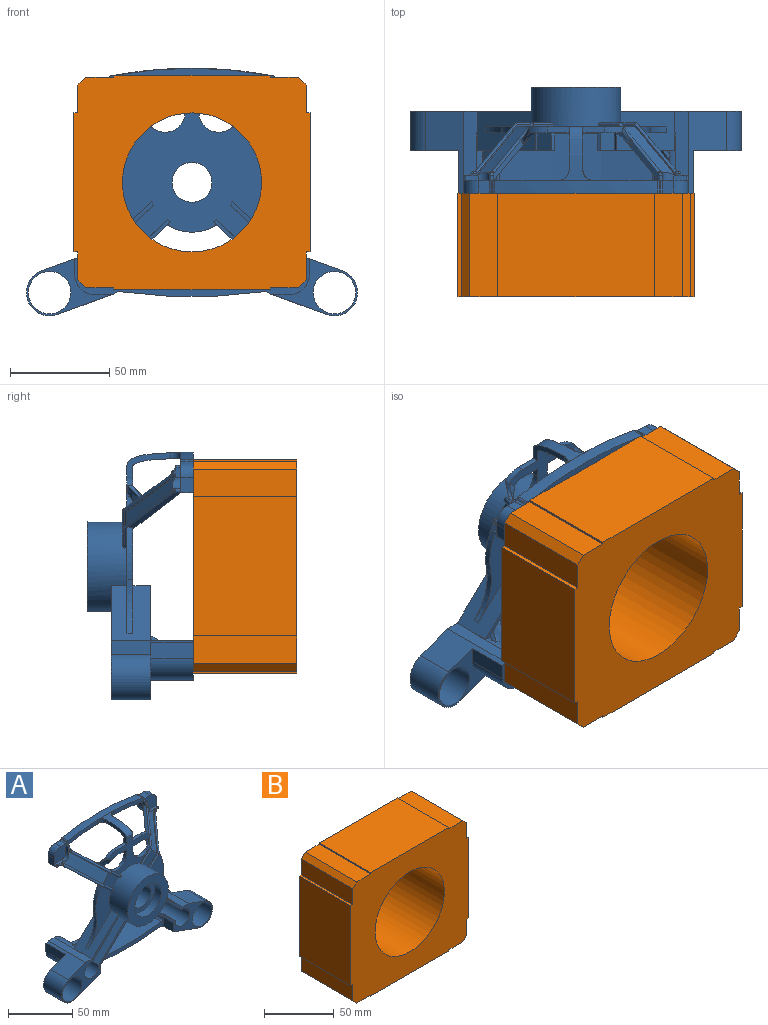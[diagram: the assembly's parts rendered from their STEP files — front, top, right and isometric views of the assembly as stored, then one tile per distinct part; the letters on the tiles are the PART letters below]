
ASSEMBLY  parts=2 mates=1
PART A: 213 faces, bbox 167x53.9x125 mm
  f0: plane 29.84x28.32mm, normal (-0.69,0,-0.73), area 460.5mm2, adj f3,f12,f15,f169,f198,f201,f211
  f1: plane 24.48x23.23mm, normal (0.69,0,0.73), area 266.4mm2, adj f92,f164,f202,f212
  f2: plane 29.8x28.28mm, normal (0.69,0,0.73), area 459.4mm2, adj f12,f15,f169,f198,f201,f202,f211
  f3: plane 30.33x28.26mm, normal (0,1,0), area 78.6mm2, adj f0,f162,f163,f169,f195,f209
  f4: bspline ~14.26x14.19mm, area 140.4mm2, adj f6,f8,f161,f205,f206,f208
  f5: bspline ~14.26x14.22mm, area 139.4mm2, adj f6,f161,f183,f205,f206,f208
  f6: plane 29.84x28.32mm, normal (0.69,0,-0.73), area 739.5mm2, adj f4,f5,f8,f12,f14,f92,f159,f183
  f7: plane 29.59x28.88mm, normal (0,1,0), area 78.6mm2, adj f68,f160,f161,f171,f183,f205
  f8: cylinder r=7.75mm len=33mm, axis (0,1,0), area 1335.2mm2, adj f4,f6,f161,f192,f204
  f9: plane 41.51x6.78mm, normal (0,0,1), area 271.3mm2, adj f11,f169,f195,f199,f201
  f10: plane 41.51x6.78mm, normal (0,0,1), area 271.3mm2, adj f11,f183,f188,f189,f192
  f11: plane 118x20mm, normal (0,1,0), area 921.6mm2, adj f9,f10,f166,f167,f168,f169,f170,f171
  f12: cylinder r=22.5mm len=45mm, axis (0,1,0), area 2748.5mm2, adj f0,f2,f6,f13,f14,f15,f16,f30
  f13: plane 53.41x25.44mm, normal (0,-1,0), area 518.2mm2, adj f12,f90,f91,f117,f135,f136,f188
  f14: plane 25.41x24.79mm, normal (0,-1,0), area 265.4mm2, adj f6,f12,f161,f207
  f15: plane 25.41x24.79mm, normal (0,-1,0), area 265.3mm2, adj f0,f2,f12,f211
  f16: plane 25.18x5.2mm, normal (0,-1,0), area 60.8mm2, adj f12,f68,f69,f70
  f17: bspline ~29.85x28.26mm, area 350.7mm2, adj f18,f19,f31,f65,f66,f149,f151,f154
  f18: plane 2x0.59mm, normal (0,-1,0), area 0.4mm2, adj f17,f65,f141
  f19: plane 2x0.59mm, normal (0,-1,0), area 0.4mm2, adj f17,f66,f140
  f20: plane 2x0.59mm, normal (0,-1,0), area 0.4mm2, adj f25,f61,f121
  f21: bspline ~29.85x28.16mm, area 455.1mm2, adj f44,f45,f46,f92,f97,f98,f102
  f22: bspline ~29.85x28.26mm, area 457.5mm2, adj f50,f51,f52,f92,f99,f100,f110
  f23: plane 2.67x2mm, normal (0,-1,0), area 2.7mm2, adj f50,f66,f67,f147
  f24: plane 3.69x2mm, normal (0,-1,0), area 4.7mm2, adj f52,f64,f65,f146
  f25: bspline ~28.25x26.47mm, area 380.2mm2, adj f20,f28,f33,f61,f62,f130,f132,f153
  f26: plane 3.69x2mm, normal (0,-1,0), area 4.7mm2, adj f44,f62,f63,f129
  f27: plane 2.67x2mm, normal (0,-1,0), area 2.7mm2, adj f46,f60,f61,f128
  f28: plane 2x0.59mm, normal (0,-1,0), area 0.4mm2, adj f25,f29,f62
  f29: cylinder r=2mm len=1.41mm, axis (0,1,0), area 1.6mm2, adj f28,f62,f124,f132,f137
  f30: plane 46.67x31.07mm, normal (0,-1,0), area 530.7mm2, adj f12,f74,f75,f76,f77,f78,f79,f80
  f31: plane 16.76x16.52mm, normal (0,-1,0), area 131.9mm2, adj f12,f17,f118,f120
  f32: plane 53.41x25.45mm, normal (0,-1,0), area 518.2mm2, adj f12,f71,f72,f73,f119,f148,f150,f195
  f33: plane 16.76x16.52mm, normal (0,-1,0), area 131.9mm2, adj f12,f25,f115,f116
  f34: plane 113x19.44mm, normal (0,-1,0), area 550.8mm2, adj f37,f38,f39,f40,f41,f42,f43,f46
  f35: plane 1x1mm, normal (0,-1,0), area 0.2mm2, adj f52,f53,f64
  f36: plane 1x1mm, normal (0,-1,0), area 0.2mm2, adj f43,f44,f63
  f37: cylinder r=216.01mm len=81.79mm, axis (0,1,0), area 534.9mm2, adj f34,f38,f58,f59
  f38: cylinder r=2mm len=6.5mm, axis (0,1,0), area 7.7mm2, adj f34,f37,f39,f59
  f39: plane 6.5x0.4mm, normal (-0.71,0,0.71), area 3.6mm2, adj f34,f38,f40,f59
  f40: cylinder r=2mm len=6.5mm, axis (0,1,0), area 10.2mm2, adj f34,f39,f41,f59
  f41: plane 6.5x5.26mm, normal (0,0,1), area 34.2mm2, adj f34,f40,f42,f59
  f42: cylinder r=7.5mm len=7.5mm, axis (0,1,0), area 76.6mm2, adj f34,f41,f43,f59
  f43: plane 7.5x6.5mm, normal (-1,0,0), area 48.7mm2, adj f34,f36,f42,f44,f59
  f44: plane 10x7.5mm, normal (0,0,-1), area 61.7mm2, adj f21,f26,f36,f43,f45,f59,f63,f97
  f45: cylinder r=7.5mm len=8.02mm, axis (0,1,0), area 94.3mm2, adj f21,f44,f46,f59
  f46: plane 10x5.49mm, normal (1,0,0), area 34.5mm2, adj f21,f27,f34,f45,f47,f59,f60,f98
  f47: cylinder r=2mm len=6.5mm, axis (0,1,0), area 18mm2, adj f34,f46,f48,f59
  f48: cylinder r=212.51mm len=79.75mm, axis (0,1,0), area 521.5mm2, adj f34,f47,f49,f59
  f49: cylinder r=2mm len=6.5mm, axis (0,1,0), area 18mm2, adj f34,f48,f50,f59
  f50: plane 10x5.49mm, normal (-1,0,0), area 34.5mm2, adj f22,f23,f34,f49,f51,f59,f67,f100
  f51: cylinder r=7.5mm len=8.02mm, axis (0,1,0), area 94.3mm2, adj f22,f50,f52,f59
  f52: plane 10x7.5mm, normal (0,0,-1), area 61.7mm2, adj f22,f24,f35,f51,f53,f59,f64,f99
  f53: plane 7.5x6.5mm, normal (1,0,0), area 48.7mm2, adj f34,f35,f52,f54,f59
  f54: cylinder r=7.5mm len=7.5mm, axis (0,1,0), area 76.6mm2, adj f34,f53,f55,f59
  f55: plane 6.5x5.26mm, normal (0,0,1), area 34.2mm2, adj f34,f54,f56,f59
  f56: cylinder r=2mm len=6.5mm, axis (0,1,0), area 10.2mm2, adj f34,f55,f57,f59
  f57: plane 6.5x0.4mm, normal (0.71,0,0.71), area 3.6mm2, adj f34,f56,f58,f59
  f58: cylinder r=2mm len=6.5mm, axis (0,1,0), area 7.7mm2, adj f34,f37,f57,f59
  f59: plane 113x20.44mm, normal (0,1,0), area 697.2mm2, adj f37,f38,f39,f40,f41,f42,f43,f44
  f60: cylinder r=1mm len=2.5mm, axis (0,1,0), area 7.9mm2, adj f27,f34,f46,f61
  f61: plane 5.48x3.5mm, normal (-1,0,0), area 14.7mm2, adj f20,f25,f27,f34,f60,f121,f126,f128
  f62: plane 6.5x3.5mm, normal (0,0,1), area 17.2mm2, adj f25,f26,f28,f29,f34,f63,f127,f129
  f63: cylinder r=1mm len=2.5mm, axis (0,1,0), area 7.9mm2, adj f26,f34,f36,f44,f62
  f64: cylinder r=1mm len=2.5mm, axis (0,1,0), area 7.9mm2, adj f24,f34,f35,f52,f65
  f65: plane 6.5x3.5mm, normal (0,0,1), area 17.2mm2, adj f17,f18,f24,f34,f64,f141,f144,f146
  f66: plane 5.48x3.5mm, normal (1,0,0), area 14.7mm2, adj f17,f19,f23,f34,f67,f140,f145,f147
  f67: cylinder r=1mm len=2.5mm, axis (0,1,0), area 7.9mm2, adj f23,f34,f50,f66
  f68: plane 29.31x27.81mm, normal (0.69,0,-0.73), area 800.2mm2, adj f7,f12,f16,f69,f92,f160,f171,f192
  f69: cylinder r=25mm len=25.18mm, axis (0,1,0), area 79.2mm2, adj f16,f68,f70,f92
  f70: plane 29.31x27.81mm, normal (-0.69,0,-0.73), area 800.2mm2, adj f12,f16,f69,f92,f164,f170,f201,f202
  f71: cylinder r=30mm len=27.1mm, axis (0,1,0), area 89.2mm2, adj f32,f72,f92,f195
  f72: cylinder r=37.5mm len=26.29mm, axis (0,1,0), area 82mm2, adj f32,f71,f73,f92,f99,f150
  f73: plane 0.07x0.06mm, normal (-0.67,0,0.74), area 0mm2, adj f32,f72,f150
  f74: plane 10.44x9.5mm, normal (-0.67,0,0.74), area 19.5mm2, adj f12,f30,f75,f92,f100,f138
  f75: cylinder r=10mm len=16.73mm, axis (0,1,0), area 69.3mm2, adj f30,f74,f76,f92
  f76: plane 4.74x3mm, normal (1,0,0), area 14.2mm2, adj f30,f75,f77,f92
  f77: plane 10.87x3mm, normal (0,0,-1), area 32.6mm2, adj f30,f76,f78,f92
  f78: cylinder r=7.5mm len=5.55mm, axis (0,1,0), area 18.7mm2, adj f30,f77,f92,f111,f114
  f79: cylinder r=12.5mm len=9.25mm, axis (0,1,0), area 31.2mm2, adj f30,f80,f92,f109,f114
  f80: plane 10.87x3mm, normal (0,0,1), area 32.6mm2, adj f30,f79,f81,f92
  f81: plane 22.18x12.25mm, normal (1,0,0), area 83.4mm2, adj f30,f80,f92,f155,f156,f157
  f82: plane 22.18x12.25mm, normal (-1,0,0), area 83.4mm2, adj f30,f83,f92,f155,f156,f158
  f83: plane 10.87x3mm, normal (0,0,1), area 32.6mm2, adj f30,f82,f84,f92
  f84: cylinder r=12.5mm len=9.25mm, axis (0,1,0), area 31.2mm2, adj f30,f83,f92,f103,f107
  f85: cylinder r=7.5mm len=5.55mm, axis (0,1,0), area 18.7mm2, adj f30,f86,f92,f101,f107
  f86: plane 10.87x3mm, normal (0,0,-1), area 32.6mm2, adj f30,f85,f87,f92
  f87: plane 4.74x3mm, normal (-1,0,0), area 14.2mm2, adj f30,f86,f88,f92
  f88: cylinder r=10mm len=16.73mm, axis (0,1,0), area 69.3mm2, adj f30,f87,f89,f92
  f89: plane 10.44x9.5mm, normal (0.67,0,0.74), area 19.5mm2, adj f12,f30,f88,f92,f98,f123
  f90: cylinder r=37.5mm len=26.39mm, axis (0,1,0), area 82.3mm2, adj f13,f91,f92,f97,f133,f134,f136
  f91: cylinder r=30mm len=27.1mm, axis (0,1,0), area 89.2mm2, adj f13,f90,f92,f188
  f92: plane 91.55x86.89mm, normal (0,1,0), area 3812.8mm2, adj f1,f6,f21,f22,f68,f69,f70,f71
  f93: cylinder r=14.5mm len=29mm, axis (0,1,0), area 637.7mm2, adj f94,f96
  f94: plane 45x45mm, normal (0,-1,0), area 929.9mm2, adj f12,f93
  f95: cylinder r=10mm len=20mm, axis (0,1,0), area 1005.3mm2, adj f92,f96
  f96: plane 29x29mm, normal (0,-1,0), area 346.4mm2, adj f93,f95
  f97: plane 25.78x20.52mm, normal (-0.66,0,-0.75), area 72.2mm2, adj f21,f44,f90,f92,f133
  f98: plane 28x19.95mm, normal (0.67,0,0.74), area 85.5mm2, adj f21,f46,f89,f104,f105,f106,f131
  f99: plane 26.81x20.43mm, normal (0.67,0,-0.74), area 98.4mm2, adj f22,f52,f72,f92,f150
  f100: plane 28x19.95mm, normal (-0.67,0,0.74), area 85.6mm2, adj f22,f50,f74,f108,f112,f113,f152
  f101: bspline ~6.29x5.94mm, area 15.6mm2, adj f85,f102,f104,f106,f107
  f102: bspline ~10.77x8.19mm, area 44mm2, adj f21,f92,f101,f103,f105,f106
  f103: bspline ~9.34x7.12mm, area 17.2mm2, adj f84,f102,f104,f105,f107
  f104: bspline ~9.52x9.23mm, area 44.3mm2, adj f98,f101,f103,f105,f106,f107
  f105: bspline ~3.15x2.78mm, area 2.4mm2, adj f98,f102,f103,f104
  f106: bspline ~3.26x2.86mm, area 4mm2, adj f98,f101,f102,f104
  f107: bspline ~5.9x5.51mm, area 3.4mm2, adj f30,f84,f85,f101,f103,f104
  f108: bspline ~10.31x8.72mm, area 43.2mm2, adj f100,f109,f111,f112,f113,f114
  f109: bspline ~8.62x7.66mm, area 16.9mm2, adj f79,f108,f110,f113,f114
  f110: bspline ~11.26x7.54mm, area 42.7mm2, adj f22,f92,f109,f111,f112,f113
  f111: bspline ~6.78x5.28mm, area 16.1mm2, adj f78,f108,f110,f112,f114
  f112: bspline ~3.12x2.62mm, area 3.7mm2, adj f100,f108,f110,f111
  f113: bspline ~3.17x2.74mm, area 2.8mm2, adj f100,f108,f109,f110
  f114: bspline ~5.51x5.14mm, area 3.1mm2, adj f30,f78,f79,f108,f109,f111
  f115: plane 10.03x9.13mm, normal (-0.67,0,-0.74), area 13.6mm2, adj f12,f33,f123,f130
  f116: plane 10.03x9.13mm, normal (0.67,0,0.74), area 13.6mm2, adj f12,f33,f122,f137
  f117: plane 10.44x9.5mm, normal (-0.67,0,-0.74), area 14.1mm2, adj f12,f13,f122,f135
  f118: plane 10.03x9.13mm, normal (-0.67,0,0.74), area 13.6mm2, adj f12,f31,f139,f149
  f119: plane 10.44x9.5mm, normal (0.67,0,-0.74), area 14.1mm2, adj f12,f32,f139,f148
  f120: plane 10.03x9.13mm, normal (0.67,0,-0.74), area 13.6mm2, adj f12,f31,f138,f151
  f121: cylinder r=2mm len=1.41mm, axis (0,1,0), area 1.6mm2, adj f20,f61,f125,f130
  f122: cylinder r=1mm len=11.79mm, axis (-0.74,0,0.67), area 43.4mm2, adj f12,f116,f117,f136
  f123: cylinder r=1mm len=11.79mm, axis (-0.74,0,0.67), area 43.4mm2, adj f12,f89,f115,f131
  f124: torus R=1mm, axis (0,-1,0), area 2.5mm2, adj f29,f127,f136
  f125: torus R=1mm, axis (0,1,0), area 2.5mm2, adj f121,f126,f131
  f126: torus R=1mm, axis (1,0,0), area 4mm2, adj f46,f61,f125,f128
  f127: torus R=1mm, axis (0,0,1), area 4mm2, adj f44,f62,f124,f129
  f128: cylinder r=1mm len=2.12mm, axis (0,-0.71,-0.71), area 5.1mm2, adj f27,f46,f61,f126
  f129: cylinder r=1mm len=2.12mm, axis (0.71,-0.71,0), area 5.1mm2, adj f26,f44,f62,f127
  f130: plane 25.5x20.02mm, normal (-0.67,0,-0.74), area 26.9mm2, adj f25,f115,f121,f131
  f131: bspline ~25.83x21.36mm, area 99.7mm2, adj f98,f123,f125,f130
  f132: bspline ~24.5x20.36mm, area 32.8mm2, adj f25,f29,f137
  f133: bspline ~24.5x20.52mm, area 2.2mm2, adj f90,f97,f134
  f134: plane 24.31x19.43mm, normal (-0.67,0,-0.74), area 26.1mm2, adj f44,f90,f133,f136
  f135: plane 1x0.83mm, normal (-0.67,0,-0.74), area 0.6mm2, adj f13,f117,f136
  f136: bspline ~26.51x21.77mm, area 101.2mm2, adj f13,f90,f122,f124,f134,f135,f137
  f137: plane 25x20.36mm, normal (0.67,0,0.74), area 20.5mm2, adj f29,f116,f132,f136
  f138: cylinder r=1mm len=11.79mm, axis (0.74,0,0.67), area 43.4mm2, adj f12,f74,f120,f152
  f139: cylinder r=1mm len=11.79mm, axis (0.74,0,0.67), area 43.4mm2, adj f12,f118,f119,f150
  f140: cylinder r=2mm len=1.41mm, axis (0,1,0), area 1.6mm2, adj f19,f66,f142,f151
  f141: cylinder r=2mm len=1.41mm, axis (0,1,0), area 1.6mm2, adj f18,f65,f143,f149
  f142: torus R=1mm, axis (0,-1,0), area 3.2mm2, adj f140,f145,f152
  f143: torus R=1mm, axis (0,1,0), area 1.7mm2, adj f141,f144,f150
  f144: torus R=1mm, axis (0,0,-1), area 4mm2, adj f52,f65,f143,f146
  f145: torus R=1mm, axis (1,0,0), area 4mm2, adj f50,f66,f142,f147
  f146: cylinder r=1mm len=2.12mm, axis (-0.71,-0.71,0), area 5.1mm2, adj f24,f52,f65,f144
  f147: cylinder r=1mm len=2.12mm, axis (0,-0.71,-0.71), area 5.1mm2, adj f23,f50,f66,f145
  f148: plane 1x0.83mm, normal (0.67,0,-0.74), area 0.6mm2, adj f32,f119,f150
  f149: plane 25.5x20.36mm, normal (-0.67,0,0.74), area 27.4mm2, adj f17,f118,f141,f150
  f150: bspline ~26.5x21.77mm, area 101.3mm2, adj f32,f72,f73,f99,f139,f143,f148,f149
  f151: plane 25.5x20.01mm, normal (0.67,0,-0.74), area 26.9mm2, adj f17,f120,f140,f152
  f152: bspline ~25.83x21.36mm, area 99.7mm2, adj f100,f138,f142,f151
  f153: cylinder r=5.5mm len=5.5mm, axis (0,1,0), area 32.1mm2, adj f25,f34,f61,f62
  f154: cylinder r=5.5mm len=5.5mm, axis (0,1,0), area 32.1mm2, adj f17,f34,f65,f66
  f155: bspline ~24x17.2mm, area 198.9mm2, adj f34,f81,f82,f92,f157,f158
  f156: bspline ~27x17.2mm, area 231.9mm2, adj f30,f34,f81,f82,f157,f158
  f157: cylinder r=5mm len=5mm, axis (0,0,1), area 23.6mm2, adj f34,f81,f155,f156
  f158: cylinder r=5mm len=5mm, axis (0,0,1), area 23.6mm2, adj f34,f82,f155,f156
  f159: cylinder r=22.5mm len=9mm, axis (0,1,0), area 18.7mm2, adj f6,f92,f188,f193
  f160: cylinder r=22.5mm len=9mm, axis (0,1,0), area 18.7mm2, adj f7,f68,f92,f161
  f161: plane 29.8x28.28mm, normal (-0.69,0,0.73), area 738.3mm2, adj f4,f5,f7,f8,f12,f14,f92,f160
  f162: cylinder r=22.5mm len=9mm, axis (0,1,0), area 18.7mm2, adj f3,f92,f163,f195
  f163: plane 24.5x23.25mm, normal (-0.69,0,-0.73), area 266.6mm2, adj f3,f92,f162,f212
  f164: cylinder r=22.5mm len=9mm, axis (0,1,0), area 18.7mm2, adj f1,f70,f92,f202
  f165: plane 80.73x8.26mm, normal (0,-1,0), area 287.9mm2, adj f166,f170,f171,f175,f176,f177,f178,f180
  f166: cylinder r=2mm len=30.5mm, axis (0,1,0), area 30.4mm2, adj f11,f165,f167,f178,f194,f196
  f167: plane 21.5x8.46mm, normal (0,0,-1), area 182mm2, adj f11,f166,f168,f194
  f168: cylinder r=10mm len=21.5mm, axis (0,1,0), area 337.7mm2, adj f11,f167,f179,f194
  f169: cylinder r=10mm len=30.5mm, axis (0,1,0), area 288.2mm2, adj f0,f2,f3,f9,f11,f170,f195,f202
  f170: plane 41.5x8.86mm, normal (-1,0,0), area 148.2mm2, adj f11,f70,f165,f169,f180,f196,f201,f202
  f171: plane 41.5x8.86mm, normal (1,0,0), area 148.2mm2, adj f7,f11,f68,f165,f182,f183,f187,f192
  f172: plane 21.5x8.07mm, normal (-1,0,0), area 173.6mm2, adj f11,f173,f186,f189
  f173: cylinder r=10mm len=21.5mm, axis (0,1,0), area 337.7mm2, adj f11,f172,f174,f186
  f174: plane 21.5x8.46mm, normal (0,0,-1), area 182mm2, adj f11,f173,f184,f186
  f175: cylinder r=2mm len=30.5mm, axis (0,1,0), area 40.3mm2, adj f11,f165,f176,f185
  f176: cylinder r=268.17mm len=73.11mm, axis (0,1,0), area 2236.8mm2, adj f11,f165,f175,f177
  f177: cylinder r=2mm len=30.5mm, axis (0,1,0), area 40.3mm2, adj f11,f165,f176,f178
  f178: plane 30.5x1.71mm, normal (-0.5,0,-0.87), area 60.1mm2, adj f11,f165,f166,f177
  f179: plane 21.5x8.07mm, normal (1,0,0), area 173.6mm2, adj f11,f168,f194,f199
  f180: cylinder r=2mm len=30.5mm, axis (0,1,0), area 87mm2, adj f11,f165,f170,f181
  f181: cylinder r=264.67mm len=76.58mm, axis (0,1,0), area 2343.9mm2, adj f11,f165,f180,f182
  f182: cylinder r=2mm len=30.5mm, axis (0,1,0), area 87mm2, adj f11,f165,f171,f181
  f183: cylinder r=10mm len=30.5mm, axis (0,1,0), area 288.2mm2, adj f5,f6,f7,f10,f11,f161,f171,f188
  f184: cylinder r=2mm len=30.5mm, axis (0,1,0), area 30.4mm2, adj f11,f165,f174,f185,f186,f187
  f185: plane 30.5x1.71mm, normal (0.5,0,-0.87), area 60.1mm2, adj f11,f165,f175,f184
  f186: plane 42.97x28.71mm, normal (0,1,0), area 255.2mm2, adj f172,f173,f174,f184,f187,f189,f190,f191
  f187: plane 27.67x20mm, normal (0.34,0,-0.94), area 585.3mm2, adj f165,f171,f184,f186,f190,f192
  f188: plane 29.37x27.87mm, normal (-0.69,0,0.73), area 704.2mm2, adj f10,f12,f13,f91,f92,f159,f183,f192
  f189: plane 41.5x19.2mm, normal (-0.34,0,0.94), area 466.8mm2, adj f10,f11,f172,f186,f190,f192
  f190: cylinder r=11.68mm len=22.65mm, axis (0,1,0), area 733.6mm2, adj f186,f187,f189,f192
  f191: cylinder r=10.68mm len=21.35mm, axis (0,1,0), area 1341.5mm2, adj f186,f192
  f192: plane 72.64x57.49mm, normal (0,-1,0), area 516.7mm2, adj f6,f8,f10,f12,f68,f161,f171,f187
  f193: plane 30.33x28.26mm, normal (0,1,0), area 78.7mm2, adj f6,f159,f183,f188,f206
  f194: plane 42.97x28.71mm, normal (0,1,0), area 255.2mm2, adj f166,f167,f168,f179,f196,f197,f199,f200
  f195: plane 29.37x27.87mm, normal (0.69,0,0.73), area 704.2mm2, adj f3,f9,f12,f32,f71,f92,f162,f169
  f196: plane 27.67x20mm, normal (-0.34,0,-0.94), area 585.3mm2, adj f165,f166,f170,f194,f197,f201
  f197: cylinder r=11.68mm len=22.65mm, axis (0,1,0), area 733.6mm2, adj f194,f196,f199,f201
  f198: cylinder r=7.75mm len=33mm, axis (0,1,0), area 1335.2mm2, adj f0,f2,f201,f203,f211
  f199: plane 41.5x19.2mm, normal (0.34,0,0.94), area 466.8mm2, adj f9,f11,f179,f194,f197,f201
  f200: cylinder r=10.68mm len=21.35mm, axis (0,1,0), area 1341.5mm2, adj f194,f201
  f201: plane 72.64x57.49mm, normal (0,-1,0), area 516.7mm2, adj f0,f2,f9,f12,f70,f170,f195,f196
  f202: plane 29.59x28.88mm, normal (0,1,0), area 78.6mm2, adj f1,f2,f70,f164,f169,f170,f210
  f203: plane 15.5x15.5mm, normal (0,-1,0), area 188.7mm2, adj f198
  f204: plane 15.5x15.5mm, normal (0,-1,0), area 188.7mm2, adj f8
  f205: plane 5x3.34mm, normal (0.69,0,-0.73), area 9.6mm2, adj f4,f5,f7,f183
  f206: plane 5x3.35mm, normal (-0.69,0,0.73), area 9.7mm2, adj f4,f5,f183,f193
  f207: cylinder r=7mm len=7.25mm, axis (0,-1,0), area 33.4mm2, adj f6,f14,f92,f161
  f208: plane 9.5x9.25mm, normal (0,-1,0), area 23.1mm2, adj f4,f5,f6,f161
  f209: plane 5x3.35mm, normal (0.69,0,0.73), area 9.7mm2, adj f3,f169,f211,f212
  f210: plane 5x3.34mm, normal (-0.69,0,-0.73), area 9.6mm2, adj f169,f202,f211,f212
  f211: bspline ~18.26x18mm, area 218.6mm2, adj f0,f2,f15,f198,f209,f210
  f212: bspline ~16.26x16.12mm, area 178.8mm2, adj f1,f92,f163,f169,f209,f210
PART B: 27 faces, bbox 119x52x108 mm
  f0: plane 52x4mm, normal (0.71,0,0.71), area 294.2mm2, adj f1,f23,f25,f26
  f1: plane 52x14mm, normal (0,0,1), area 728mm2, adj f0,f2,f25,f26
  f2: plane 52x1mm, normal (1,0,0), area 52mm2, adj f1,f3,f25,f26
  f3: plane 79x52mm, normal (0,0,1), area 4108mm2, adj f2,f4,f25,f26
  f4: plane 52x1mm, normal (-1,0,0), area 52mm2, adj f3,f5,f25,f26
  f5: plane 52x14mm, normal (0,0,1), area 728mm2, adj f4,f6,f25,f26
  f6: plane 52x4mm, normal (-0.71,0,0.71), area 294.2mm2, adj f5,f7,f25,f26
  f7: plane 52x14mm, normal (-1,0,0), area 728mm2, adj f6,f8,f25,f26
  f8: plane 52x2mm, normal (0,0,1), area 104mm2, adj f7,f9,f25,f26
  f9: plane 70x52mm, normal (-1,0,0), area 3640mm2, adj f8,f10,f25,f26
  f10: plane 52x2mm, normal (0,0,-1), area 104mm2, adj f9,f11,f25,f26
  f11: plane 52x14mm, normal (-1,0,0), area 728mm2, adj f10,f12,f25,f26
  f12: plane 52x4mm, normal (-0.71,0,-0.71), area 294.2mm2, adj f11,f13,f25,f26
  f13: plane 52x14mm, normal (0,0,-1), area 728mm2, adj f12,f14,f25,f26
  f14: plane 52x1mm, normal (-1,0,0), area 52mm2, adj f13,f15,f25,f26
  f15: plane 79x52mm, normal (0,0,-1), area 4108mm2, adj f14,f16,f25,f26
  f16: plane 52x1mm, normal (1,0,0), area 52mm2, adj f15,f17,f25,f26
  f17: plane 52x14mm, normal (0,0,-1), area 728mm2, adj f16,f18,f25,f26
  f18: plane 52x4mm, normal (0.71,0,-0.71), area 294.2mm2, adj f17,f19,f25,f26
  f19: plane 52x14mm, normal (1,0,0), area 728mm2, adj f18,f20,f25,f26
  f20: plane 52x2mm, normal (0,0,-1), area 104mm2, adj f19,f21,f25,f26
  f21: plane 70x52mm, normal (1,0,0), area 3640mm2, adj f20,f22,f25,f26
  f22: plane 52x2mm, normal (0,0,1), area 104mm2, adj f21,f23,f25,f26
  f23: plane 52x14mm, normal (1,0,0), area 728mm2, adj f0,f22,f25,f26
  f24: cylinder r=35mm len=70mm, axis (0,1,0), area 11435.4mm2, adj f25,f26
  f25: plane 119x108mm, normal (0,-1,0), area 8747.5mm2, adj f0,f1,f2,f3,f4,f5,f6,f7
  f26: plane 119x108mm, normal (0,1,0), area 8747.5mm2, adj f0,f1,f2,f3,f4,f5,f6,f7
PLACE A rot(axis=(0,0,1),180deg) t=(-19.58,16.97,13.01)mm
PLACE B rot(axis=(0,-1,0),180deg) t=(-19.58,16.97,13.01)mm
MATE fastened A.f95 <-> B.f24  axis (0,-1,0) through (-19.58,47.47,13.01)mm
